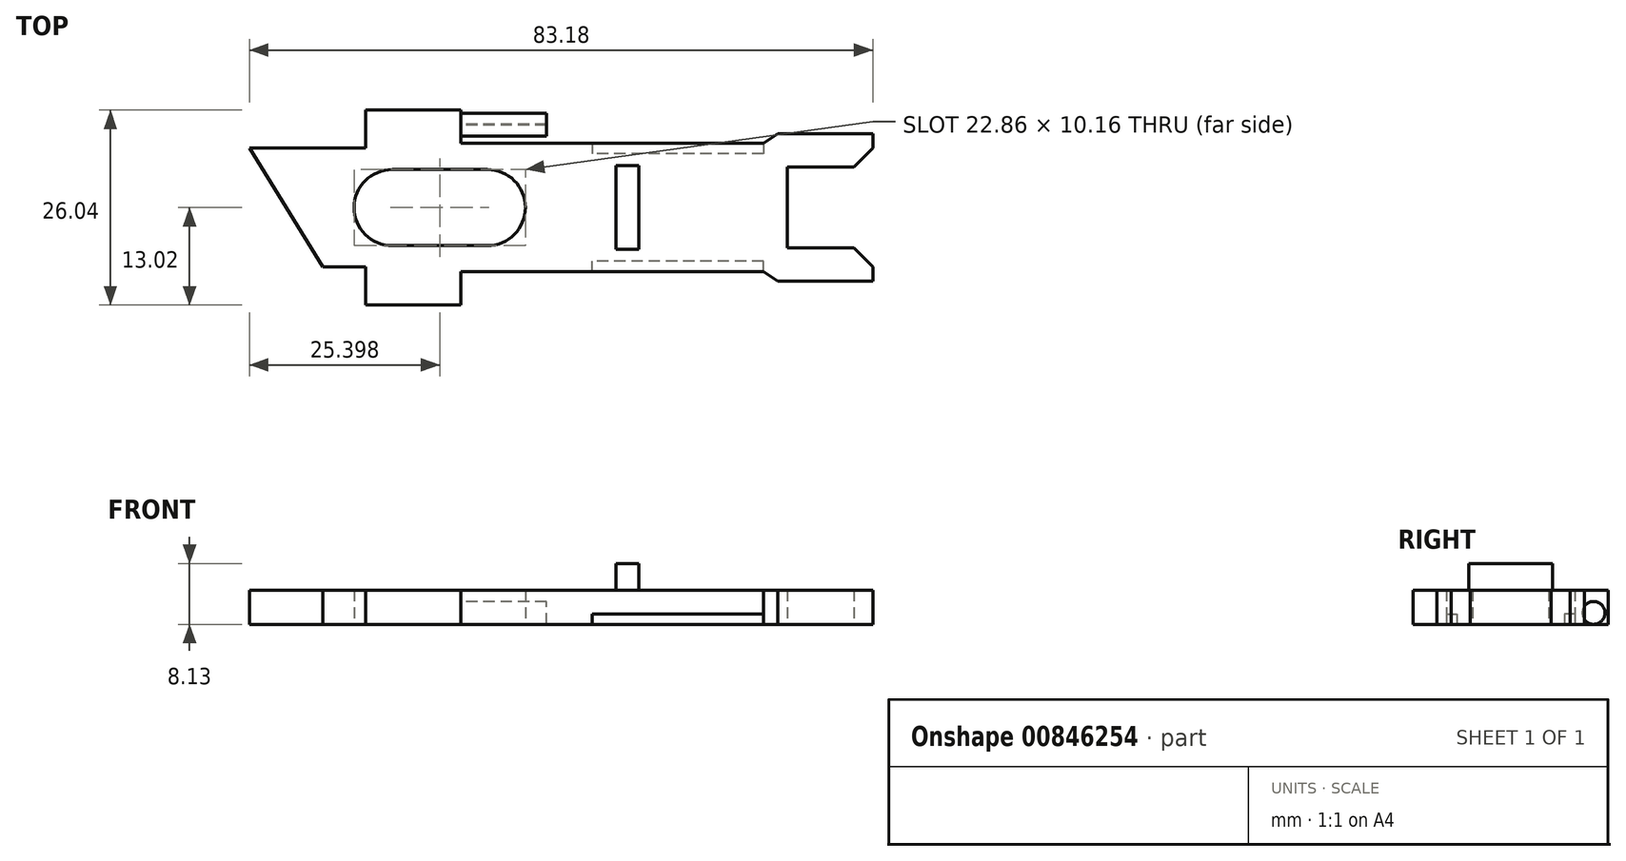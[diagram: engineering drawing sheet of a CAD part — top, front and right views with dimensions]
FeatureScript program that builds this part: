
annotation { "Feature Type Name" : "Feature", "Feature Type Description" : "" }
export const myFeature = defineFeature(function(context is Context, id is Id, definition is map)
    precondition{}
    {
        {
            var Q0;
            Q0=qCreatedBy(makeId("Top.planeOp"),FACE);
            var sketch = newSketch(context, id + "F0", { "sketchPlane" : qUnion([Q0])});
            skLineSegment(sketch, "E0", {"start": v(31.34, -9.84) * mm, "end": v(18.64, -9.84) * mm});
            skLineSegment(sketch, "E1", {"start": v(18.64, -9.84) * mm, "end": v(16.74, -8.57) * mm});
            skLineSegment(sketch, "E2", {"start": v(16.74, -8.57) * mm, "end": v(-23.65, -8.57) * mm});
            skLineSegment(sketch, "E3", {"start": v(-23.65, -8.57) * mm, "end": v(-23.65, -13.02) * mm});
            skLineSegment(sketch, "E4", {"start": v(-23.65, -13.02) * mm, "end": v(-36.35, -13.02) * mm});
            skLineSegment(sketch, "E5", {"start": v(-36.35, -13.02) * mm, "end": v(-36.35, -7.94) * mm});
            skLineSegment(sketch, "E6", {"start": v(-36.35, -7.94) * mm, "end": v(-42.06, -7.94) * mm});
            skLineSegment(sketch, "E7", {"start": v(-42.06, -7.94) * mm, "end": v(-51.84, 7.94) * mm});
            skLineSegment(sketch, "E8", {"start": v(-51.84, 7.94) * mm, "end": v(-36.35, 7.94) * mm});
            skLineSegment(sketch, "E9", {"start": v(-36.35, 7.94) * mm, "end": v(-36.35, 13.02) * mm});
            skLineSegment(sketch, "E10", {"start": v(-36.35, 13.02) * mm, "end": v(-23.65, 13.02) * mm});
            skLineSegment(sketch, "E11", {"start": v(-23.65, 13.02) * mm, "end": v(-23.65, 8.57) * mm});
            skLineSegment(sketch, "E12", {"start": v(-23.65, 8.57) * mm, "end": v(16.74, 8.57) * mm});
            skLineSegment(sketch, "E13", {"start": v(16.74, 8.57) * mm, "end": v(18.64, 9.84) * mm});
            skLineSegment(sketch, "E14", {"start": v(18.64, 9.84) * mm, "end": v(31.34, 9.84) * mm});
            skLineSegment(sketch, "E15", {"start": v(31.34, 9.84) * mm, "end": v(31.34, 7.94) * mm});
            skLineSegment(sketch, "E16", {"start": v(31.34, 7.94) * mm, "end": v(28.8, 5.4) * mm});
            skLineSegment(sketch, "E17", {"start": v(28.8, 5.4) * mm, "end": v(19.91, 5.4) * mm});
            skLineSegment(sketch, "E18", {"start": v(19.91, 5.4) * mm, "end": v(19.91, -5.4) * mm});
            skLineSegment(sketch, "E19", {"start": v(19.91, -5.4) * mm, "end": v(28.8, -5.4) * mm});
            skLineSegment(sketch, "E20", {"start": v(28.8, -5.4) * mm, "end": v(31.34, -7.94) * mm});
            skLineSegment(sketch, "E21", {"start": v(31.34, -7.94) * mm, "end": v(31.34, -9.84) * mm});
            skPoint(sketch, "E22", {"position": v(-20.1, 0) * mm});
            skPoint(sketch, "E23", {"position": v(-32.8, 0) * mm});
            skArc(sketch, "E24", {"start": v(-20.1, 5.08) * mm, "mid": v(-15.01, 0) * mm, "end": v(-20.1, -5.08) * mm});
            skArc(sketch, "E25", {"start": v(-32.8, 5.08) * mm, "mid": v(-37.87, 0) * mm, "end": v(-32.8, -5.08) * mm});
            skLineSegment(sketch, "E26", {"start": v(-32.8, 5.08) * mm, "end": v(-20.1, 5.08) * mm});
            skLineSegment(sketch, "E27", {"start": v(-32.8, -5.08) * mm, "end": v(-20.1, -5.08) * mm});
            skPoint(sketch, "E28", {"position": v(-1.42, 0) * mm});
            skLineSegment(sketch, "E29.bottom", {"start": v(-2.95, 5.59) * mm, "end": v(0.1, 5.59) * mm});
            skLineSegment(sketch, "E29.top", {"start": v(-2.95, -5.59) * mm, "end": v(0.1, -5.59) * mm});
            skLineSegment(sketch, "E29.left", {"start": v(-2.95, 5.59) * mm, "end": v(-2.95, -5.59) * mm});
            skLineSegment(sketch, "E29.right", {"start": v(0.1, 5.59) * mm, "end": v(0.1, -5.59) * mm});
            skSolve(sketch);
        }
        {
            var Q0;
            Q0=qSketchRegion(id+"F0",true);
            extrude(context, id + "F1", {"entities" : qUnion([Q0]), "depth" : 4.57 * mm, "offsetDistance" : 25.4 * mm});
        }
        {
            var Q0;
            Q0=makeQuery(id+"F0.imprint","IMPRINT",FACE,{"disambiguationData":[TD([[makeQuery(id+"F0.imprint","IMPRINT",EDGE,{"derivedFrom":sQuery(id+"F0.wireOp",EDGE,"E29.bottom")}),-1.0]])]});
            extrude(context, id + "F2", {"entities" : qUnion([Q0]), "operationType" : NewBodyOperationType.ADD, "depth" : 8.13 * mm, "offsetDistance" : 25.4 * mm});
        }
        {
            var Q0;
            Q0=makeQuery(id+"F1.opExtrude","SWEPT_FACE",FACE,{"disambiguationData":[OSD([sQuery(id+"F0.wireOp",EDGE,"E11")])]});
            var sketch = newSketch(context, id + "F3", { "sketchPlane" : qUnion([Q0])});
            skPoint(sketch, "E30.centerSnap0", {"position": v(-10.8, 0) * mm});
            skCircle(sketch, "E31", {"center": v(11.08, 1.52) * mm, "radius": 1.53 * mm});
            skSolve(sketch);
        }
        {
            var Q0;
            {var subQ0=sQuery(id+"F3.wireOp",EDGE,"E30");var subQ1=makeQuery(id+"F1.opExtrude","CAP_EDGE",EDGE,{"disambiguationData":[OSD([sQuery(id+"F0.wireOp",EDGE,"E3")])],"isStart":true});var subQ2=makeQuery(id+"F3.imprint","INTERSECT",VERTEX,{"disambiguationData":[OD(0.0)],"derivedFrom":[subQ1,subQ0]});Q0=makeQuery(id+"F3.imprint","IMPRINT",FACE,{"disambiguationData":[TD([[makeQuery(id+"F3.imprint","IMPRINT",EDGE,{"disambiguationData":[TD([[subQ2,-1.0]])],"derivedFrom":subQ0}),1.0]])]});}
            var Q1;
            {var subQ0=sQuery(id+"F3.wireOp",EDGE,"E31");var subQ1=makeQuery(id+"F1.opExtrude","CAP_EDGE",EDGE,{"disambiguationData":[OSD([sQuery(id+"F0.wireOp",EDGE,"E11")])],"isStart":true});var subQ2=makeQuery(id+"F3.imprint","INTERSECT",VERTEX,{"disambiguationData":[OD(0.0)],"derivedFrom":[subQ1,subQ0]});Q1=makeQuery(id+"F3.imprint","IMPRINT",FACE,{"disambiguationData":[TD([[makeQuery(id+"F3.imprint","IMPRINT",EDGE,{"disambiguationData":[TD([[subQ2,-1.0]])],"derivedFrom":subQ0}),1.0]])]});}
            extrude(context, id + "F4", {"entities" : qUnion([Q0, Q1]), "operationType" : NewBodyOperationType.ADD, "depth" : 11.43 * mm, "offsetDistance" : 25.4 * mm});
        }
        {
            var Q0;
            {var subQ0=sQuery(id+"F0.wireOp",EDGE,"E3");var subQ1=sQuery(id+"F0.wireOp",EDGE,"E29.right");var subQ2=sQuery(id+"F0.wireOp",EDGE,"E29.left");var subQ3=sQuery(id+"F0.wireOp",EDGE,"E29.top");var subQ4=sQuery(id+"F0.wireOp",EDGE,"E29.bottom");Q0=makeQuery(id+"F4.boolean.opBoolean","MERGE",FACE,{"derivedFrom":[makeQuery(id+"F2.boolean.opBoolean","MERGE",FACE,{"derivedFrom":[makeQuery(id+"F1.opExtrude","CAP_FACE",FACE,{"disambiguationData":[OSD([sQuery(id+"F0.wireOp",EDGE,"E0"),sQuery(id+"F0.wireOp",EDGE,"E1"),sQuery(id+"F0.wireOp",EDGE,"E2"),subQ0,sQuery(id+"F0.wireOp",EDGE,"E4"),sQuery(id+"F0.wireOp",EDGE,"E5"),sQuery(id+"F0.wireOp",EDGE,"E6"),sQuery(id+"F0.wireOp",EDGE,"E7"),sQuery(id+"F0.wireOp",EDGE,"E8"),sQuery(id+"F0.wireOp",EDGE,"E9"),sQuery(id+"F0.wireOp",EDGE,"E10"),sQuery(id+"F0.wireOp",EDGE,"E11"),sQuery(id+"F0.wireOp",EDGE,"E12"),sQuery(id+"F0.wireOp",EDGE,"E13"),sQuery(id+"F0.wireOp",EDGE,"E14"),sQuery(id+"F0.wireOp",EDGE,"E15"),sQuery(id+"F0.wireOp",EDGE,"E16"),sQuery(id+"F0.wireOp",EDGE,"E17"),sQuery(id+"F0.wireOp",EDGE,"E18"),sQuery(id+"F0.wireOp",EDGE,"E19"),sQuery(id+"F0.wireOp",EDGE,"E20"),sQuery(id+"F0.wireOp",EDGE,"E21"),sQuery(id+"F0.wireOp",EDGE,"E24"),sQuery(id+"F0.wireOp",EDGE,"E25"),sQuery(id+"F0.wireOp",EDGE,"E26"),sQuery(id+"F0.wireOp",EDGE,"E27"),subQ4,subQ3,subQ2,subQ1])],"isStart":true}),makeQuery(id+"F2.opExtrude","CAP_FACE",FACE,{"disambiguationData":[OSD([subQ4,subQ3,subQ2,subQ1])],"isStart":true})]}),makeQuery(id+"F4.opExtrude","SWEPT_FACE",FACE,{"disambiguationData":[OSD([subQ0])]})]});}
            var sketch = newSketch(context, id + "F5", { "sketchPlane" : qUnion([Q0])});
            skLineSegment(sketch, "E32.bottom", {"start": v(16.74, -8.57) * mm, "end": v(-6.12, -8.57) * mm});
            skLineSegment(sketch, "E32.top", {"start": v(16.74, -7.18) * mm, "end": v(-6.12, -7.18) * mm});
            skLineSegment(sketch, "E32.left", {"start": v(16.74, -8.57) * mm, "end": v(16.74, -7.18) * mm});
            skLineSegment(sketch, "E32.right", {"start": v(-6.12, -8.57) * mm, "end": v(-6.12, -7.18) * mm});
            skLineSegment(sketch, "E33.bottom", {"start": v(16.74, 8.57) * mm, "end": v(-6.12, 8.57) * mm});
            skLineSegment(sketch, "E33.top", {"start": v(16.74, 7.18) * mm, "end": v(-6.12, 7.18) * mm});
            skLineSegment(sketch, "E33.left", {"start": v(16.74, 8.57) * mm, "end": v(16.74, 7.18) * mm});
            skLineSegment(sketch, "E33.right", {"start": v(-6.12, 8.57) * mm, "end": v(-6.12, 7.18) * mm});
            skSolve(sketch);
        }
        {
            var Q0;
            Q0=makeQuery(id+"F5.imprint","IMPRINT",FACE,{"disambiguationData":[TD([[makeQuery(id+"F5.imprint","IMPRINT",EDGE,{"derivedFrom":sQuery(id+"F5.wireOp",EDGE,"E33.bottom")}),1.0]])]});
            extrude(context, id + "F6", {"entities" : qUnion([Q0]), "operationType" : NewBodyOperationType.REMOVE, "oppositeDirection" : true, "depth" : 1.4 * mm, "offsetDistance" : 25.4 * mm});
        }
        {
            var Q0;
            Q0=makeQuery(id+"F5.imprint","IMPRINT",FACE,{"disambiguationData":[TD([[makeQuery(id+"F5.imprint","IMPRINT",EDGE,{"derivedFrom":sQuery(id+"F5.wireOp",EDGE,"E32.bottom")}),1.0]])]});
            extrude(context, id + "F7", {"entities" : qUnion([Q0]), "operationType" : NewBodyOperationType.REMOVE, "oppositeDirection" : true, "depth" : 1.4 * mm, "offsetDistance" : 25.4 * mm});
        }
    });
